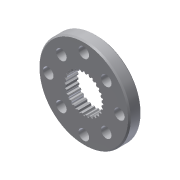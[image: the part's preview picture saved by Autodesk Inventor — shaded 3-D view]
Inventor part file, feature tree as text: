
AUTODESK INVENTOR PART (.ipt)
format: ipt  version: 2013 (Build 170138000, 138)  size: 222,208 bytes
history: native  units: in
note: dims shown in document units (in); Inventor stores cm internally (conversion verified against a paired STEP export)
features: chamfer x1, other x1, imported_body x1
ambient origin geometry x8: Origin, YZ Plane, XZ Plane, XY Plane, X Axis, Y Axis, Z Axis, Center Point
feature tree (3):
  chamfer  "Chamfer1"  [1 undecoded]
  other  "217-2724-002 Rev11"
  imported_body  "Base1"
note: 1 required parameter value undecoded (feature->parameter linkage not recoverable at this tier; creation-order binding heuristic only, values carry confidence <= 0.55)
